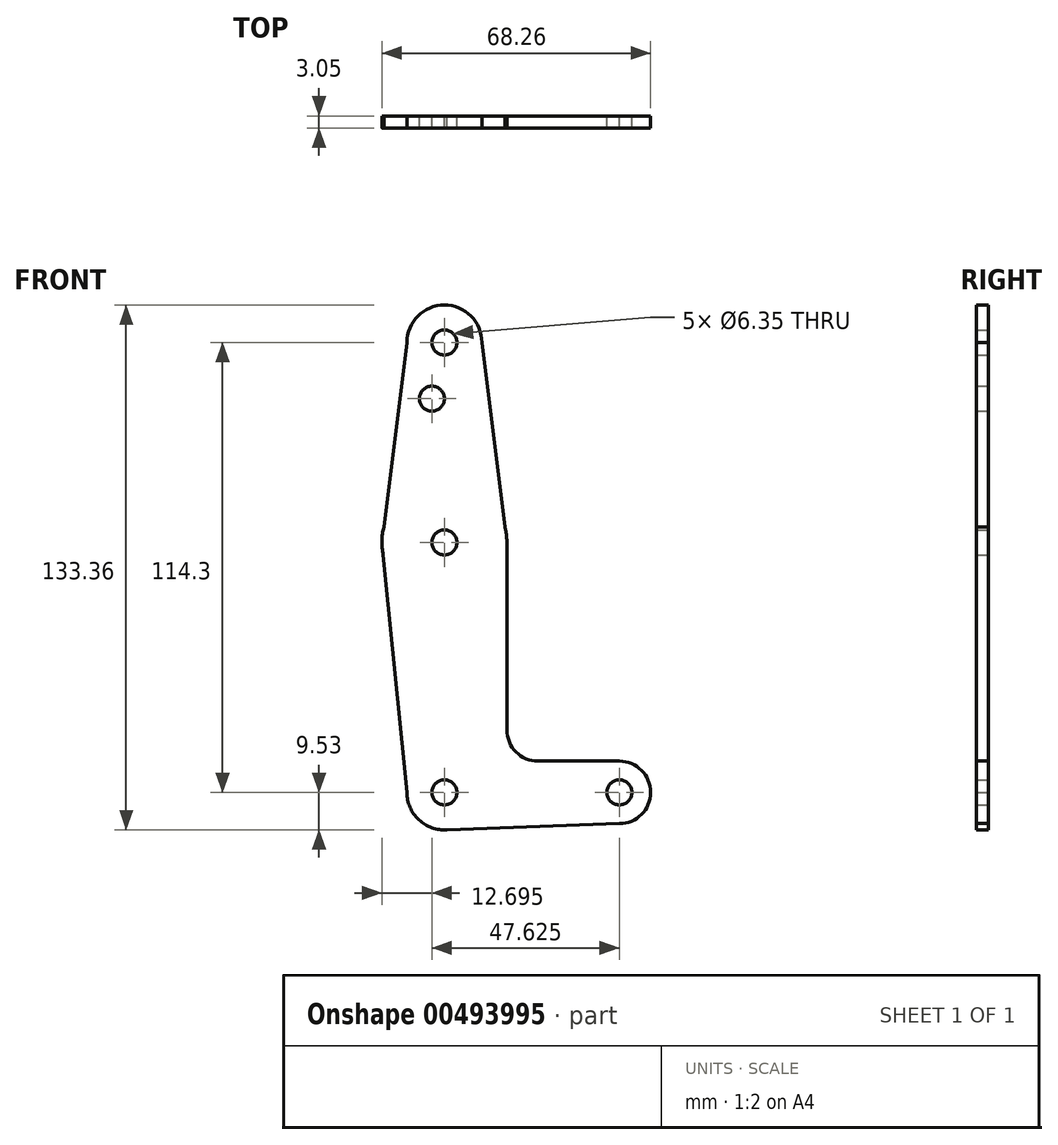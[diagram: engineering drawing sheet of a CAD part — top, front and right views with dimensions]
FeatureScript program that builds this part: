
annotation { "Feature Type Name" : "Feature", "Feature Type Description" : "" }
export const myFeature = defineFeature(function(context is Context, id is Id, definition is map)
    precondition{}
    {
        {
            var Q0;
            Q0=qCreatedBy(makeId("Front.planeOp"),FACE);
            var sketch = newSketch(context, id + "F0", { "sketchPlane" : qUnion([Q0])});
            skLineSegment(sketch, "E0", {"start": v(0, 0) * mm, "end": v(0, 114.3) * mm, "construction": true});
            skLineSegment(sketch, "E1", {"start": v(0, 0) * mm, "end": v(44.45, 0) * mm, "construction": true});
            skCircle(sketch, "E2", {"center": v(0, 114.3) * mm, "radius": 9.53 * mm});
            skCircle(sketch, "E3", {"center": v(0, 0) * mm, "radius": 9.53 * mm});
            skCircle(sketch, "E4", {"center": v(44.45, 0) * mm, "radius": 7.94 * mm});
            skCircle(sketch, "E5", {"center": v(0, 63.5) * mm, "radius": 15.88 * mm});
            skLineSegment(sketch, "E6", {"start": v(9.53, 114.3) * mm, "end": v(15.88, 63.5) * mm});
            skLineSegment(sketch, "E7", {"start": v(-9.53, 114.3) * mm, "end": v(-15.88, 63.5) * mm});
            skLineSegment(sketch, "E8", {"start": v(-15.88, 63.5) * mm, "end": v(-9.53, 0) * mm});
            skLineSegment(sketch, "E9", {"start": v(15.88, 63.5) * mm, "end": v(15.88, 15.89) * mm});
            skLineSegment(sketch, "E10", {"start": v(23.83, 7.94) * mm, "end": v(44.45, 7.94) * mm});
            skLineSegment(sketch, "E11", {"start": v(0, -9.53) * mm, "end": v(44.45, -7.94) * mm});
            skCircle(sketch, "E12", {"center": v(0, 114.3) * mm, "radius": 3.18 * mm});
            skCircle(sketch, "E13", {"center": v(0, 63.5) * mm, "radius": 3.18 * mm});
            skCircle(sketch, "E14", {"center": v(0, 0) * mm, "radius": 3.18 * mm});
            skCircle(sketch, "E15", {"center": v(44.45, 0) * mm, "radius": 3.18 * mm});
            skArc(sketch, "E16.filletArc", {"start": v(15.88, 15.89) * mm, "mid": v(18.2, 10.27) * mm, "end": v(23.83, 7.94) * mm});
            skCircle(sketch, "E17", {"center": v(-3.18, 100.03) * mm, "radius": 3.18 * mm});
            skSolve(sketch);
        }
        {
            var Q0;
            Q0 = qSketchRegion(id + "F0", true);
            extrude(context, id + "F1", {"entities" : qUnion([Q0]), "depth" : 3.05 * mm});
        }
    });
